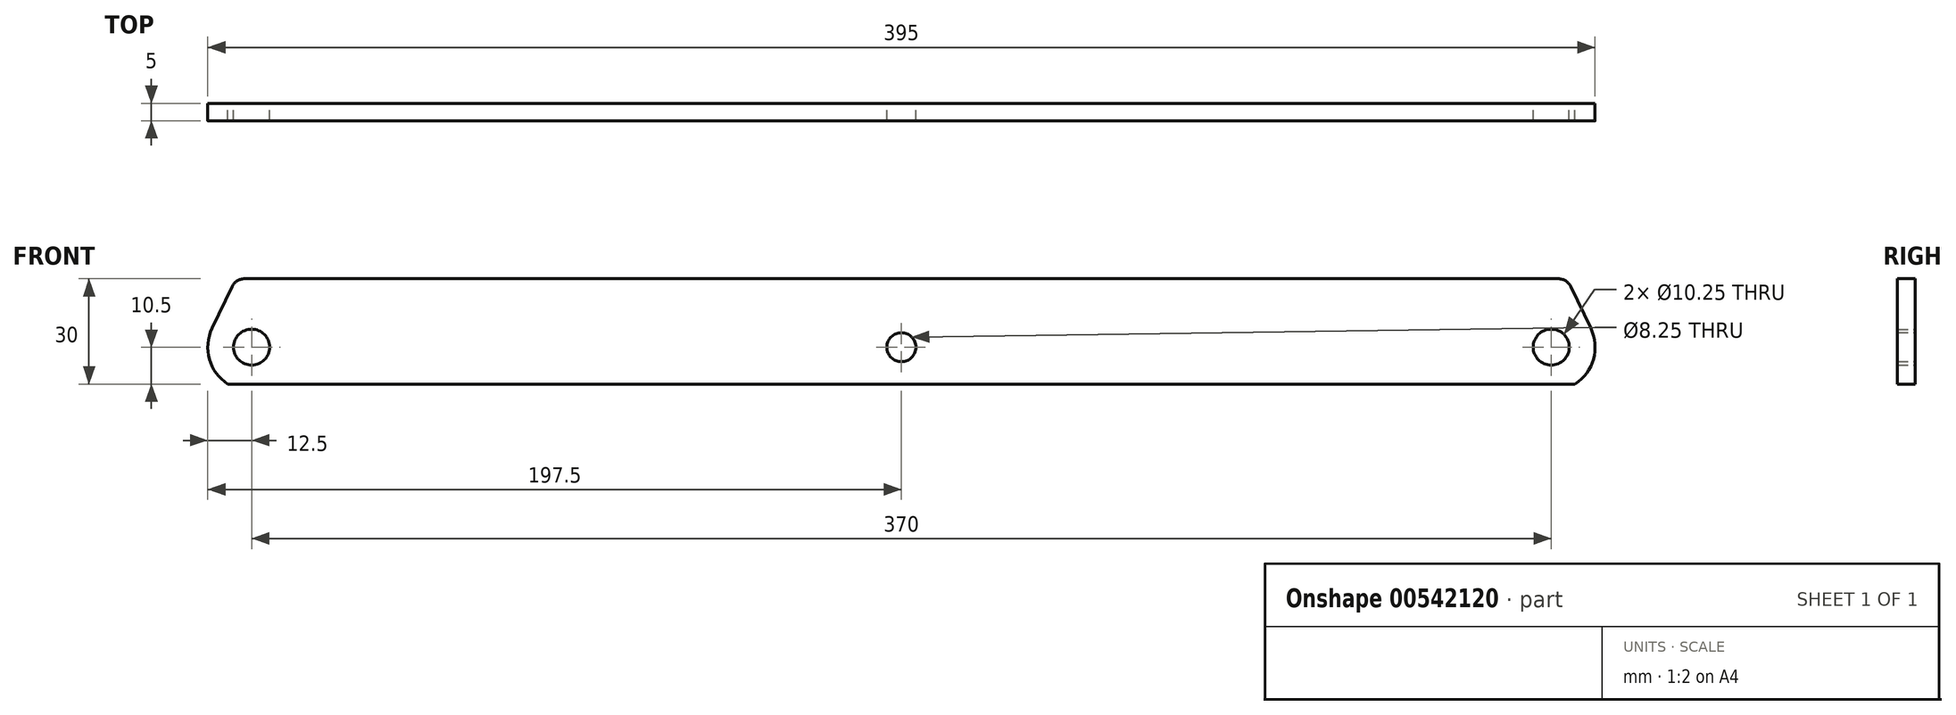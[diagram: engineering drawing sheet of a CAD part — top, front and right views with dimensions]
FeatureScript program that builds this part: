
annotation { "Feature Type Name" : "Feature", "Feature Type Description" : "" }
export const myFeature = defineFeature(function(context is Context, id is Id, definition is map)
    precondition{}
    {
        {
            var Q0;
            Q0=qCreatedBy(makeId("Front.planeOp"),FACE);
            var sketch = newSketch(context, id + "F0", { "sketchPlane" : qUnion([Q0])});
            skLineSegment(sketch, "E0", {"start": v(0, 0) * mm, "end": v(-191.78, 0) * mm});
            skLineSegment(sketch, "E1", {"start": v(-187, 30) * mm, "end": v(0, 30) * mm});
            skLineSegment(sketch, "E2", {"start": v(0, 30) * mm, "end": v(0, 14.63) * mm});
            skPoint(sketch, "E3.visualSharp", {"position": v(-130.15, 30) * mm});
            skArc(sketch, "E4", {"start": v(-196.27, 15.9) * mm, "mid": v(-197.03, 7.1) * mm, "end": v(-191.78, 0) * mm});
            skLineSegment(sketch, "E5", {"start": v(-197.5, 28.62) * mm, "end": v(-197.5, -7.34) * mm, "construction": true});
            skLineSegment(sketch, "E6", {"start": v(-196.27, 15.9) * mm, "end": v(-190.6, 27.73) * mm});
            skPoint(sketch, "E7.visualSharp", {"position": v(-189.52, 30) * mm});
            skArc(sketch, "E7.filletArc", {"start": v(-187, 30) * mm, "mid": v(-189.13, 29.38) * mm, "end": v(-190.6, 27.73) * mm});
            skCircle(sketch, "E8", {"center": v(-185, 10.5) * mm, "radius": 5.12 * mm});
            skArc(sketch, "E9", {"start": v(0, 14.63) * mm, "mid": v(-4.12, 10.5) * mm, "end": v(0, 6.38) * mm});
            skLineSegment(sketch, "E10.trimOffspring", {"start": v(0, 6.38) * mm, "end": v(0, 0) * mm});
            skSolve(sketch);
        }
        {
            var Q0;
            Q0=makeQuery(id+"F0.imprint","IMPRINT",FACE,{"disambiguationData":[TD([[makeQuery(id+"F0.imprint","IMPRINT",EDGE,{"derivedFrom":sQuery(id+"F0.wireOp",EDGE,"E0")}),-1.0]])]});
            extrude(context, id + "F1", {"entities" : qUnion([Q0]), "depth" : 5 * mm, "offsetDistance" : 25 * mm});
        }
        {
            var Q0;
            Q0=makeQuery(id+"F1.opExtrude","SWEPT_BODY",BODY,{"disambiguationData":[OSD([sQuery(id+"F0.wireOp",EDGE,"E0"),sQuery(id+"F0.wireOp",EDGE,"E1"),sQuery(id+"F0.wireOp",EDGE,"E2"),sQuery(id+"F0.wireOp",EDGE,"E4"),sQuery(id+"F0.wireOp",EDGE,"E6"),sQuery(id+"F0.wireOp",EDGE,"E7.filletArc"),sQuery(id+"F0.wireOp",EDGE,"E8"),sQuery(id+"F0.wireOp",EDGE,"E9"),sQuery(id+"F0.wireOp",EDGE,"E10.trimOffspring")])]});
            var Q1;
            Q1=qCreatedBy(makeId("Right.planeOp"),FACE);
            mirror(context, id + "F2", {"operationType" : NewBodyOperationType.ADD, "entities" : qUnion([Q0]), "mirrorPlane" : qUnion([Q1])});
        }
    });
